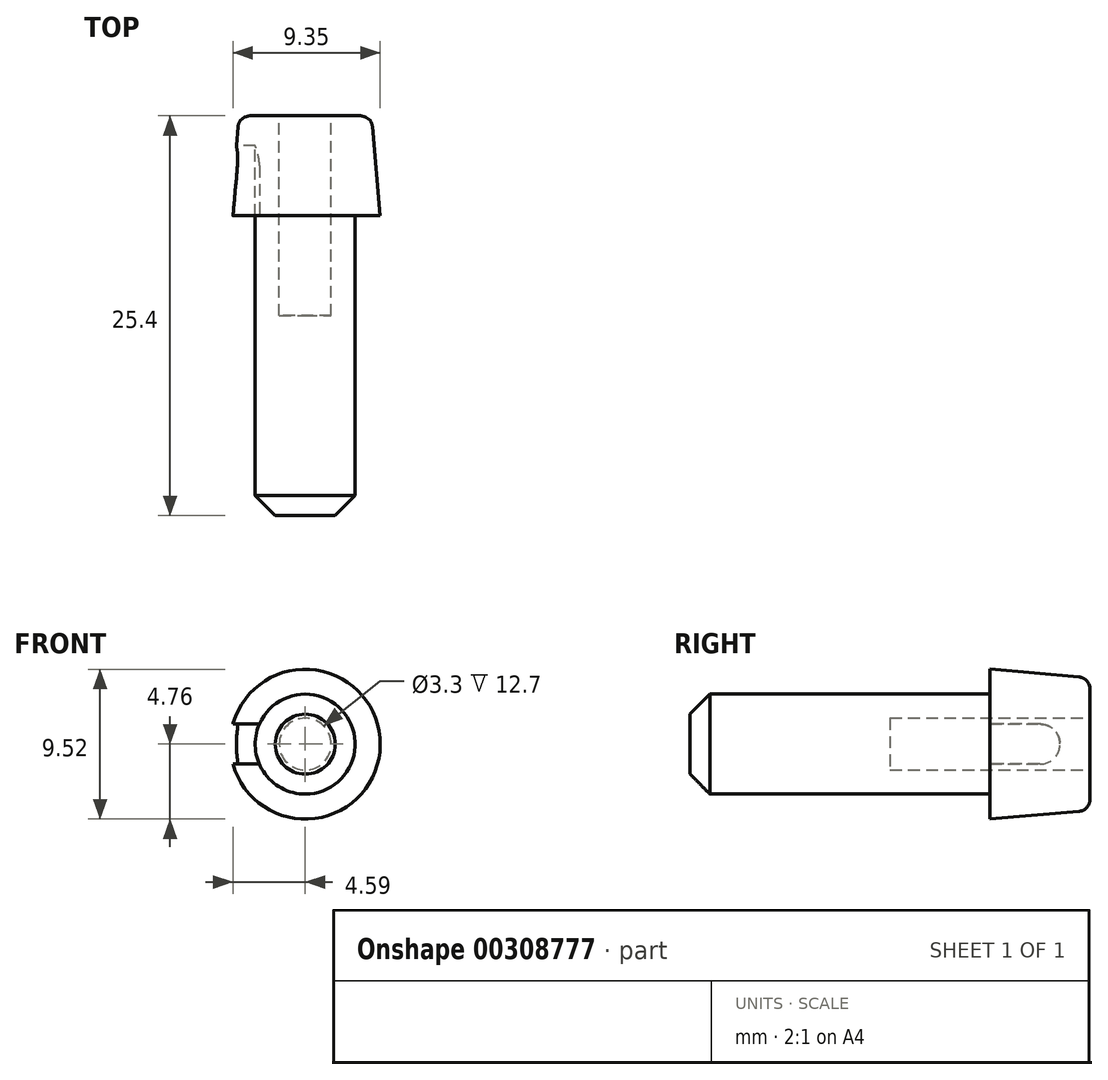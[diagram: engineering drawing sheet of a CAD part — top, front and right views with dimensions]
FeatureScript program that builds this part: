
annotation { "Feature Type Name" : "Feature", "Feature Type Description" : "" }
export const myFeature = defineFeature(function(context is Context, id is Id, definition is map)
    precondition{}
    {
        {
            var Q0;
            Q0=qCreatedBy(makeId("Front.planeOp"),FACE);
            var sketch = newSketch(context, id + "F0", { "sketchPlane" : qUnion([Q0])});
            skCircle(sketch, "E0", {"center": v(0, 0) * mm, "radius": 4.76 * mm});
            skSolve(sketch);
        }
        {
            var Q0;
            Q0=makeQuery(id+"F0.imprint","IMPRINT",FACE,{"disambiguationData":[TD([[makeQuery(id+"F0.imprint","IMPRINT",EDGE,{"derivedFrom":sQuery(id+"F0.wireOp",EDGE,"E0")}),1.0]])]});
            extrude(context, id + "F1", {"entities" : qUnion([Q0]), "oppositeDirection" : true, "depth" : 6.35 * mm, "hasDraft" : true, "draftAngle" : 5 * degree, "draftPullDirection" : true});
        }
        {
            var Q0;
            Q0=makeQuery(id+"F1.opExtrude","CAP_FACE",FACE,{"disambiguationData":[OSD([sQuery(id+"F0.wireOp",EDGE,"E0")])],"isStart":true});
            var sketch = newSketch(context, id + "F2", { "sketchPlane" : qUnion([Q0])});
            skCircle(sketch, "E1", {"center": v(0, 0) * mm, "radius": 3.18 * mm});
            skSolve(sketch);
        }
        {
            var Q0;
            Q0=makeQuery(id+"F2.imprint","IMPRINT",FACE,{"disambiguationData":[TD([[makeQuery(id+"F2.imprint","IMPRINT",EDGE,{"derivedFrom":sQuery(id+"F2.wireOp",EDGE,"E1")}),1.0]])]});
            extrude(context, id + "F3", {"entities" : qUnion([Q0]), "operationType" : NewBodyOperationType.ADD, "depth" : 19.05 * mm});
        }
        {
            var Q0;
            Q0=makeQuery(id+"F1.opExtrude","CAP_FACE",FACE,{"disambiguationData":[OSD([sQuery(id+"F0.wireOp",EDGE,"E0")])],"isStart":false});
            var sketch = newSketch(context, id + "F4", { "sketchPlane" : qUnion([Q0])});
            skCircle(sketch, "E2", {"center": v(0, 0) * mm, "radius": 1.65 * mm});
            skSolve(sketch);
        }
        {
            var Q0;
            Q0=makeQuery(id+"F4.imprint","IMPRINT",FACE,{"disambiguationData":[TD([[makeQuery(id+"F4.imprint","IMPRINT",EDGE,{"derivedFrom":sQuery(id+"F4.wireOp",EDGE,"E2")}),1.0]])]});
            extrude(context, id + "F5", {"entities" : qUnion([Q0]), "operationType" : NewBodyOperationType.REMOVE, "oppositeDirection" : true, "depth" : 12.7 * mm});
        }
        {
            var Q0;
            Q0=makeQuery(id+"F3.opExtrude","CAP_EDGE",EDGE,{"disambiguationData":[OSD([sQuery(id+"F2.wireOp",EDGE,"E1")])],"isStart":false});
            chamfer(context, id + "F6", {"entities" : qUnion([Q0]), "width" : 1.27 * mm, "tangentPropagation" : true});
        }
        {
            var Q0;
            Q0=makeQuery(id+"F1.opExtrude","CAP_EDGE",EDGE,{"disambiguationData":[OSD([sQuery(id+"F0.wireOp",EDGE,"E0")])],"isStart":false});
            fillet(context, id + "F7", {"entities" : qUnion([Q0]), "radius" : 0.76 * mm, "tangentPropagation" : true, "allowEdgeOverflow" : false});
        }
        {
            var Q0;
            Q0=makeQuery(id+"F1.opExtrude","CAP_FACE",FACE,{"disambiguationData":[OSD([sQuery(id+"F0.wireOp",EDGE,"E0")])],"isStart":true});
            var sketch = newSketch(context, id + "F8", { "sketchPlane" : qUnion([Q0])});
            skLineSegment(sketch, "E3", {"start": v(-2.9, 1.27) * mm, "end": v(-4.6, 1.27) * mm});
            skLineSegment(sketch, "E4", {"start": v(-2.9, -1.27) * mm, "end": v(-4.6, -1.27) * mm});
            skSolve(sketch);
        }
        {
            var Q0;
            {var subQ0=sQuery(id+"F8.wireOp",EDGE,"E3");Q0=makeQuery(id+"F8.imprint","IMPRINT",FACE,{"disambiguationData":[TD([[makeQuery(id+"F8.imprint","IMPRINT",EDGE,{"derivedFrom":subQ0}),1.0]])]});}
            extrude(context, id + "F9", {"entities" : qUnion([Q0]), "operationType" : NewBodyOperationType.REMOVE, "oppositeDirection" : true, "depth" : 4.44 * mm});
        }
        {
            var Q0;
            Q0=makeQuery(id+"F9.boolean.opBoolean","COPY",EDGE,{"derivedFrom":makeQuery(id+"F9.opExtrude","CAP_EDGE",EDGE,{"disambiguationData":[OSD([sQuery(id+"F8.wireOp",EDGE,"E3")])],"isStart":false})});
            var Q1;
            Q1=makeQuery(id+"F9.boolean.opBoolean","COPY",EDGE,{"derivedFrom":makeQuery(id+"F9.opExtrude","CAP_EDGE",EDGE,{"disambiguationData":[OSD([sQuery(id+"F8.wireOp",EDGE,"E4")])],"isStart":false})});
            fillet(context, id + "F10", {"entities" : qUnion([Q0, Q1]), "radius" : 1.27 * mm, "tangentPropagation" : true, "allowEdgeOverflow" : false});
        }
    });
